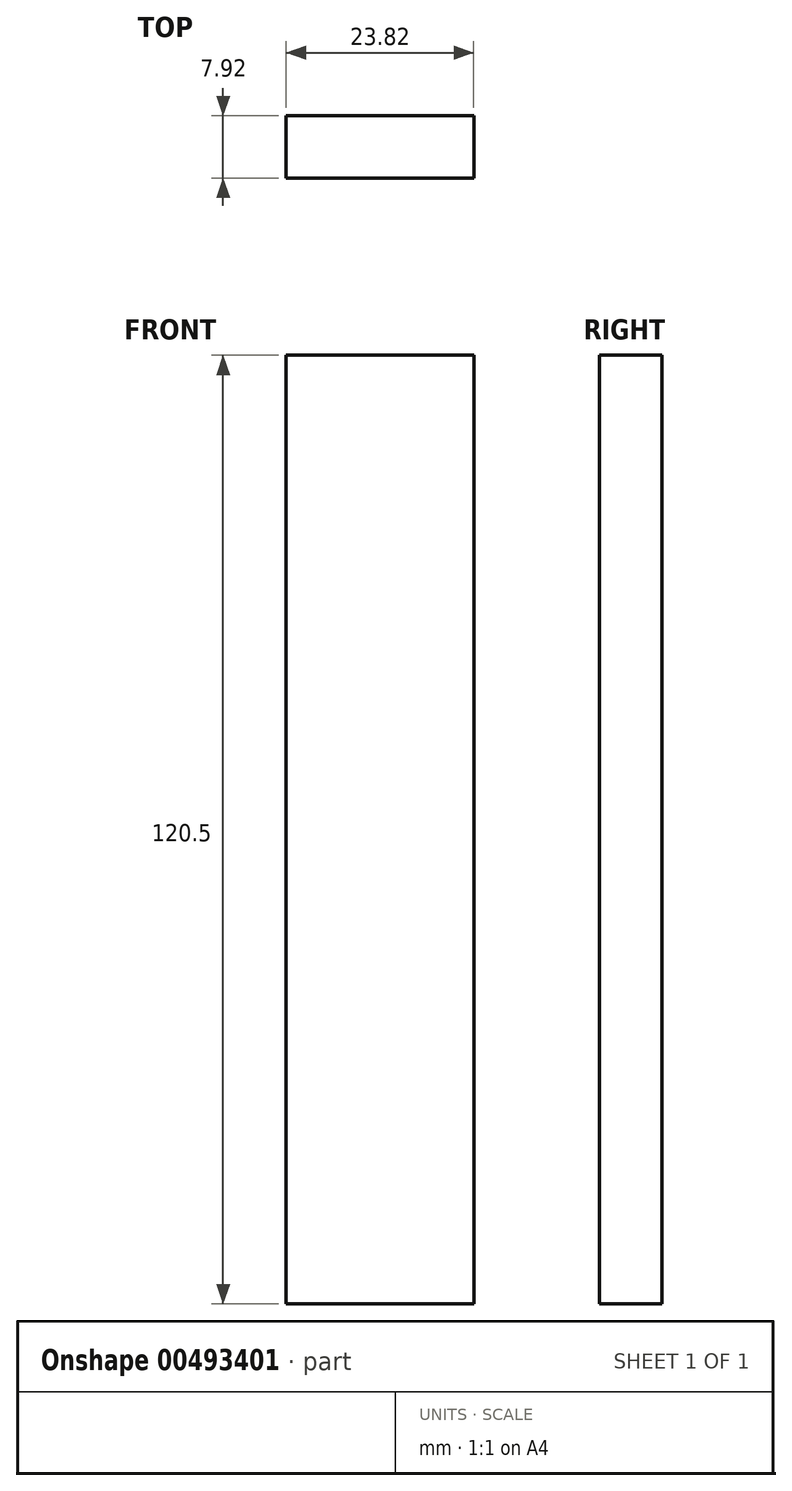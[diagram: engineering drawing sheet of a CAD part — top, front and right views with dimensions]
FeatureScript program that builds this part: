
annotation { "Feature Type Name" : "Feature", "Feature Type Description" : "" }
export const myFeature = defineFeature(function(context is Context, id is Id, definition is map)
    precondition{}
    {
        {
            var Q0;
            Q0=qCreatedBy(makeId("Front.planeOp"),FACE);
            var sketch = newSketch(context, id + "F0", { "sketchPlane" : qUnion([Q0])});
            skLineSegment(sketch, "E0.bottom", {"start": v(-11.91, 60.25) * mm, "end": v(11.91, 60.25) * mm});
            skLineSegment(sketch, "E0.top", {"start": v(-11.91, -60.25) * mm, "end": v(11.91, -60.25) * mm});
            skLineSegment(sketch, "E0.left", {"start": v(-11.91, 60.25) * mm, "end": v(-11.91, -60.25) * mm});
            skLineSegment(sketch, "E0.right", {"start": v(11.91, 60.25) * mm, "end": v(11.91, -60.25) * mm});
            skPoint(sketch, "E0.middle", {"position": v(0, 0) * mm});
            skSolve(sketch);
        }
        {
            var Q0;
            Q0=makeQuery(id+"F0.imprint","IMPRINT",FACE,{"disambiguationData":[TD([[makeQuery(id+"F0.imprint","IMPRINT",EDGE,{"derivedFrom":sQuery(id+"F0.wireOp",EDGE,"E0.bottom")}),-1.0]])]});
            extrude(context, id + "F1", {"entities" : qUnion([Q0]), "depth" : 7.92 * mm});
        }
    });
